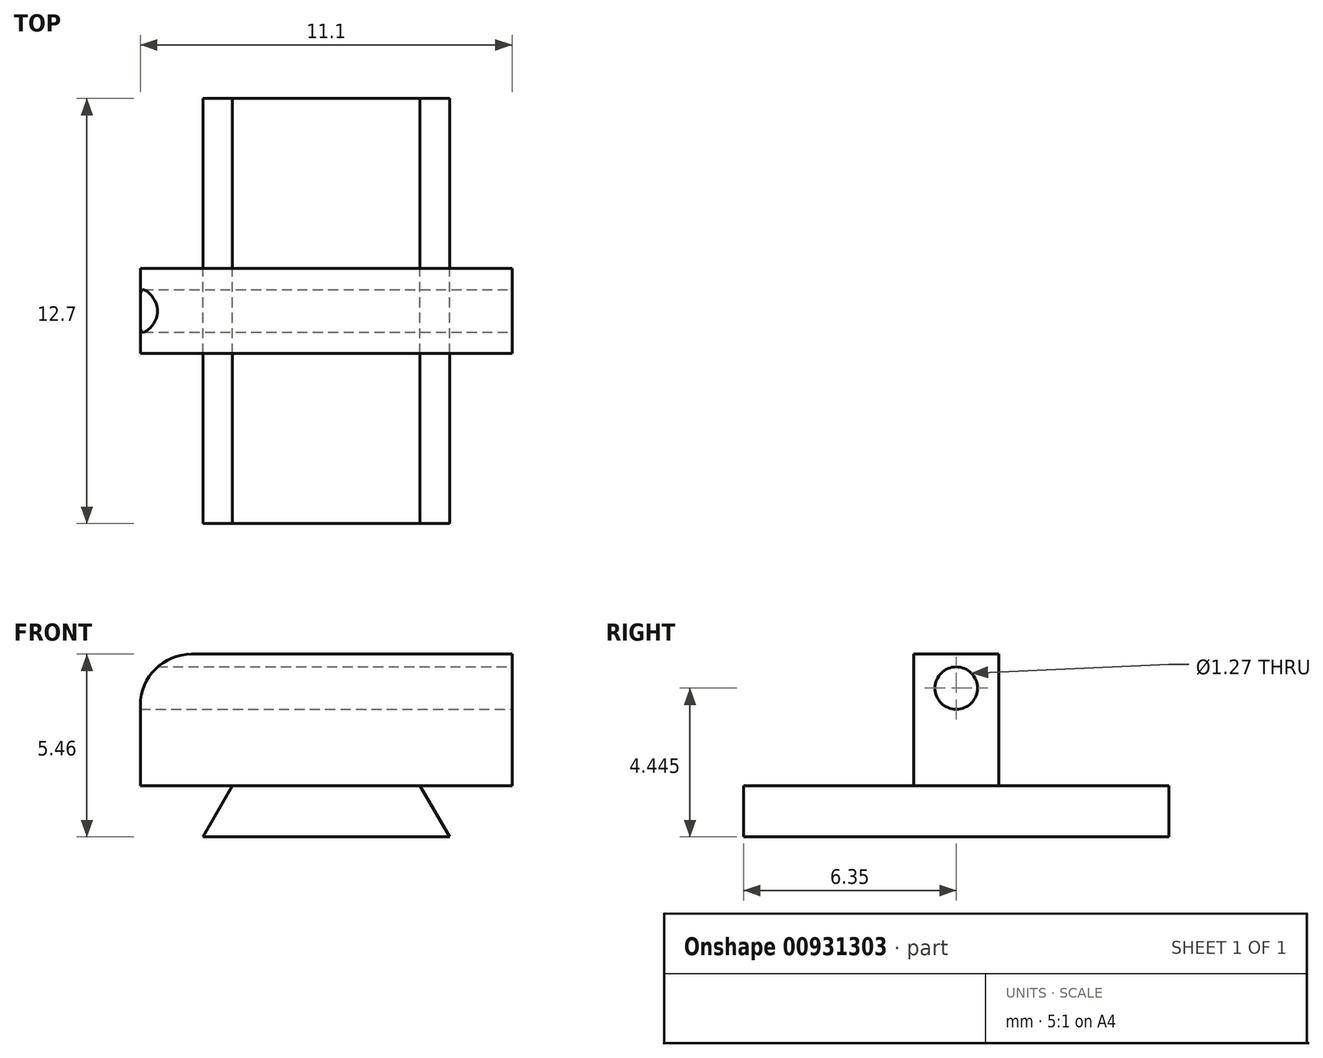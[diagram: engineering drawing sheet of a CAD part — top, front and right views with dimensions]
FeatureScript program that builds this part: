
annotation { "Feature Type Name" : "Feature", "Feature Type Description" : "" }
export const myFeature = defineFeature(function(context is Context, id is Id, definition is map)
    precondition{}
    {
        {
            var Q0;
            Q0=qCreatedBy(makeId("Front.planeOp"),FACE);
            var sketch = newSketch(context, id + "F0", { "sketchPlane" : qUnion([Q0])});
            skLineSegment(sketch, "E0", {"start": v(-3.74, 0) * mm, "end": v(3.62, 0) * mm});
            skLineSegment(sketch, "E1", {"start": v(3.62, 0) * mm, "end": v(2.74, 1.52) * mm});
            skLineSegment(sketch, "E2", {"start": v(2.74, 1.52) * mm, "end": v(5.49, 1.52) * mm});
            skLineSegment(sketch, "E3", {"start": v(5.49, 1.52) * mm, "end": v(5.49, 5.46) * mm});
            skLineSegment(sketch, "E4", {"start": v(5.49, 5.46) * mm, "end": v(-5.6, 5.46) * mm});
            skLineSegment(sketch, "E5", {"start": v(-5.6, 5.46) * mm, "end": v(-5.6, 1.52) * mm});
            skLineSegment(sketch, "E6", {"start": v(-5.6, 1.52) * mm, "end": v(-2.86, 1.52) * mm});
            skLineSegment(sketch, "E7", {"start": v(-2.86, 1.52) * mm, "end": v(-3.74, 0) * mm});
            skSolve(sketch);
        }
        {
            var Q0;
            Q0=makeQuery(id+"F0.imprint","IMPRINT",FACE,{"disambiguationData":[TD([[makeQuery(id+"F0.imprint","IMPRINT",EDGE,{"derivedFrom":sQuery(id+"F0.wireOp",EDGE,"E0")}),1.0]])]});
            extrude(context, id + "F1", {"entities" : qUnion([Q0]), "depth" : 12.7 * mm, "offsetDistance" : 25.4 * mm});
        }
        {
            var Q0;
            Q0=makeQuery(id+"F1.opExtrude","SWEPT_FACE",FACE,{"disambiguationData":[OSD([sQuery(id+"F0.wireOp",EDGE,"E3")])]});
            var sketch = newSketch(context, id + "F2", { "sketchPlane" : qUnion([Q0])});
            skLineSegment(sketch, "E8", {"start": v(-12.7, 1.52) * mm, "end": v(-7.62, 1.52) * mm});
            skLineSegment(sketch, "E9", {"start": v(-7.62, 1.52) * mm, "end": v(-7.62, 5.46) * mm});
            skLineSegment(sketch, "E10", {"start": v(-7.62, 5.46) * mm, "end": v(-5.08, 5.46) * mm});
            skLineSegment(sketch, "E11", {"start": v(-5.08, 5.46) * mm, "end": v(-5.08, 1.52) * mm});
            skLineSegment(sketch, "E12", {"start": v(-5.08, 1.52) * mm, "end": v(0, 1.52) * mm});
            skLineSegment(sketch, "E13", {"start": v(0, 1.52) * mm, "end": v(0, 0) * mm});
            skLineSegment(sketch, "E14", {"start": v(0, 0) * mm, "end": v(-12.7, 0) * mm});
            skLineSegment(sketch, "E15", {"start": v(-12.7, 0) * mm, "end": v(-12.7, 1.52) * mm});
            skSolve(sketch);
        }
        {
            var Q0;
            {var subQ0=sQuery(id+"F2.wireOp",EDGE,"E9");Q0=makeQuery(id+"F2.imprint","IMPRINT",FACE,{"disambiguationData":[TD([[makeQuery(id+"F2.imprint","IMPRINT",EDGE,{"derivedFrom":subQ0}),-1.0]])]});}
            var Q1;
            {var subQ1=sQuery(id+"F2.wireOp",EDGE,"E8");Q1=makeQuery(id+"F2.imprint","IMPRINT",FACE,{"disambiguationData":[TD([[makeQuery(id+"F2.imprint","IMPRINT",EDGE,{"derivedFrom":subQ1}),-1.0]])]});}
            extrude(context, id + "F3", {"entities" : qUnion([Q0, Q1]), "operationType" : NewBodyOperationType.INTERSECT, "oppositeDirection" : true, "depth" : 25.4 * mm, "offsetDistance" : 25.4 * mm});
        }
        {
            var Q0;
            Q0=makeQuery(id+"F1.opExtrude","SWEPT_EDGE",EDGE,{"disambiguationData":[OSD([sQuery(id+"F0.wireOp",EDGE,"E4"),sQuery(id+"F0.wireOp",EDGE,"E5")])]});
            fillet(context, id + "F4", {"entities" : qUnion([Q0]), "radius" : 1.52 * mm, "tangentPropagation" : true, "allowEdgeOverflow" : false});
        }
        {
            var Q0;
            Q0=makeQuery(id+"F1.opExtrude","SWEPT_FACE",FACE,{"disambiguationData":[OSD([sQuery(id+"F0.wireOp",EDGE,"E3")])]});
            var sketch = newSketch(context, id + "F5", { "sketchPlane" : qUnion([Q0])});
            skCircle(sketch, "E16", {"center": v(-6.35, 4.45) * mm, "radius": 0.64 * mm});
            skSolve(sketch);
        }
        {
            var Q0;
            Q0=makeQuery(id+"F5.imprint","IMPRINT",FACE,{"disambiguationData":[TD([[makeQuery(id+"F5.imprint","IMPRINT",EDGE,{"derivedFrom":sQuery(id+"F5.wireOp",EDGE,"E16")}),1.0]])]});
            extrude(context, id + "F6", {"entities" : qUnion([Q0]), "operationType" : NewBodyOperationType.REMOVE, "oppositeDirection" : true, "depth" : 25.4 * mm, "offsetDistance" : 25.4 * mm});
        }
    });
